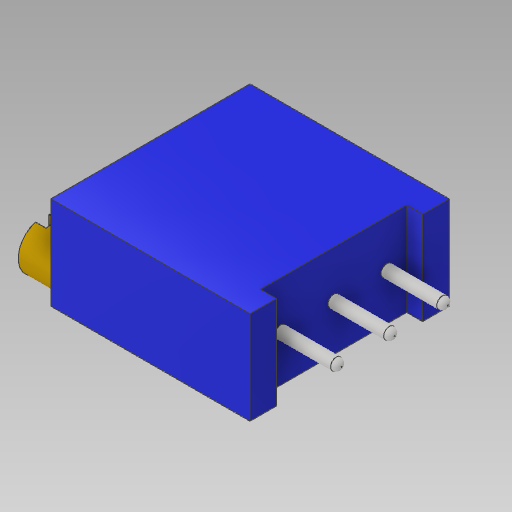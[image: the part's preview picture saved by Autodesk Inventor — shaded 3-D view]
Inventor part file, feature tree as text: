
AUTODESK INVENTOR PART (.ipt)
format: ipt  version: 2020 (Build 240168000, 168)  size: 162,816 bytes
history: native  units: in
note: dims shown in document units (in); Inventor stores cm internally (conversion verified against a paired STEP export)
features: extrude x4, sketch x4, fillet x1
ambient origin geometry x8: Origin, YZ Plane, XZ Plane, XY Plane, X Axis, Y Axis, Z Axis, Center Point
bodies: Solid1 (feature_tree)
feature tree (9):
  extrude  "Extrusion1"  Depth=0.375in
  extrude  "Extrusion2"  Depth=0.03in
  extrude  "Extrusion3"  Depth=0.175in
  extrude  "Extrusion4"  Depth=0.01in
  fillet  "Fillet1"  Radius=0.115in
  sketch  "Sketch1"  dims[d0=0.375in d1=0.375in]
  sketch  "Sketch2"  dims[d2=0.275in d3=0.03in]
  sketch  "Sketch3"  dims[d4=0.175in d5=0.0in d6=0.022in]
  sketch  "Sketch4"  dims[d7=0.1in d8=0.1in d9=0.115in d10=0.0in d11=0.09in d12=0.046in d13=0.046in d14=0.0625in d15=0.0in d16=0.02in d17=0.025in d18=0.0625in d19=0.0in d20=0.01in]
